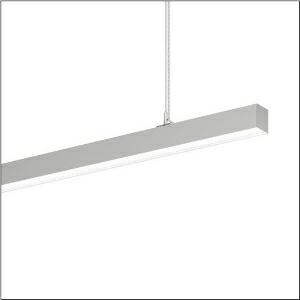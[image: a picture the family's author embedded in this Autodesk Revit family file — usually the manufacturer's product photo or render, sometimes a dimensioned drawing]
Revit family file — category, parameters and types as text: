
# Revit family: silica_r__21_51mx33tat7s_6391
name_source: partatom
category: Lighting Fixtures
units: mm (PartAtom-declared; Revit-internal decimal feet)

## family parameters
Cut with Voids When Loaded = No
Host = Face
Light Source = No
Part Type = Normal
Room Calculation Point = No
Round Connector Dimension = Use Diameter
Shared = No

## types (1)
- --- (1 x LED, 5740 lm, 53.8 W, 6500K)
    Apparent Load = 54 VA
    CIE Flux Codes = 78 96 99 56 100
    Color Rendering = 80
    Color Temperature = 6500K
    Default Elevation = 1800 mm
    Description = Silica® 21, office luminaire, primary optical cover: prismatic diffuser, of PMMA, CAT 2 (L<= 3000cd/m²), light emission: direct/indirect distribution, primary light characteristic: symmetric, installation type: suspended mounting, LED, rated luminous flux: 5.740lm, luminous efficacy: 102lm/W, light colour: 8tw, colour temperature: 2700..6500K, control gear: ECG DALI, with terminal, 3+2-pole, max. 2.5mm², mains connection: 220..240V, AC, 50/60Hz, rated input power: 56.5W, luminaire housing, of aluminium, metallic grey (RAL 9006), length: 1.204mm, width: 53mm, height: 53mm, protection rating (complete): IP20, insulation class (complete): insulation class I (protective earthing), certification: CE, permissible operating ambient temperature: 0..+35°C, standard: EN 50419, packaging unit: 1 piece
    Height = 53 mm
    Lamp = 1 x LED
    Lamp Light Flux = 5740 lm
    Lamp Power = 53.8 W
    Lamp count = 1
    Length = 1204 mm
    Luminous efficacy = 107 lm/W
    Manufacturer = Siteco
    ModVariant = No
    Model = 51MX33TAT7S
    Mounting Place = Ceiling
    Mounting Type = Pendant
    Number of Poles = 1
    OnlyDefault = Yes
    Power Factor = 1
    Product Name = Silica® 21
    Product group = office luminaire | ceiling pendant
    ProductGroupID = 905
    Protection Class = Protection class I
    Protection Degree = IP 20
    RLX_Detail_Level = 1
    RlxData = <blob elided: 20201 chars, md5=ddacc8fa>
    Socket = socket
    Standby Power = 0 W
    System Light Flux = 5740 lm
    System Power = 54 W
    Type Comments = individual setting
    Type Image = l_1251727.jpg
    URL = http://relux.com
    VarID = @adj_045837
    Voltage = 0 V
    Weight = 0.00 kg
    Width = 53 mm

## geometry (parser evidence)
native form markers: Blend x4, Sweep x12
no freeform markers — native parametric forms only
